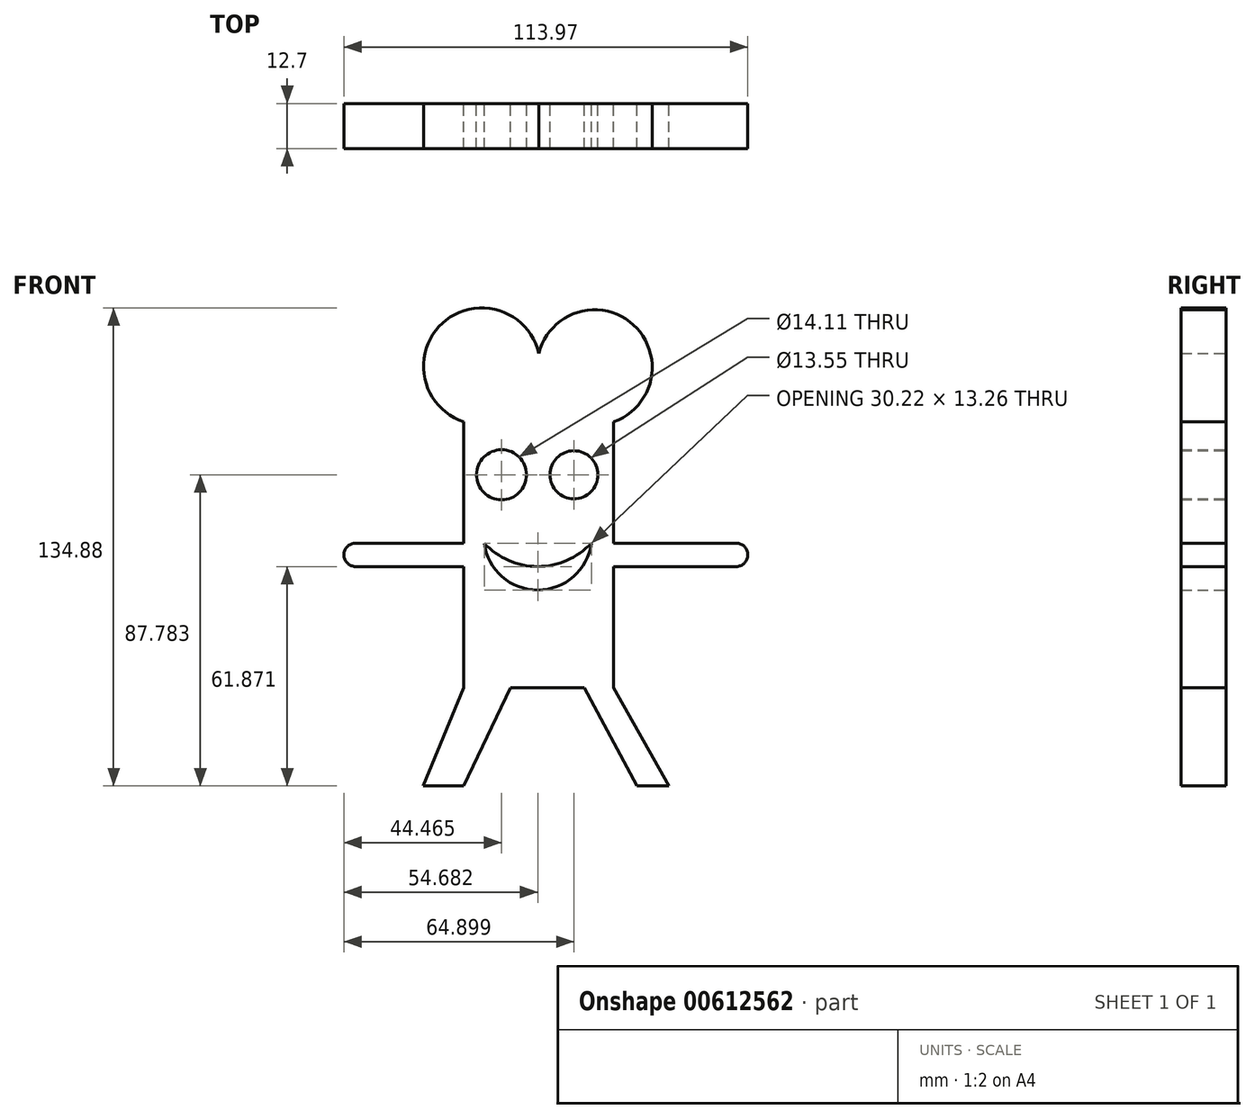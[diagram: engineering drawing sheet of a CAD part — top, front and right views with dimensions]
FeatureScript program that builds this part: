
annotation { "Feature Type Name" : "Feature", "Feature Type Description" : "" }
export const myFeature = defineFeature(function(context is Context, id is Id, definition is map)
    precondition{}
    {
        {
            var Q0;
            Q0=qCreatedBy(makeId("Front.planeOp"),FACE);
            var sketch = newSketch(context, id + "F0", { "sketchPlane" : qUnion([Q0])});
            skLineSegment(sketch, "E0.bottom", {"start": v(21.15, 37.56) * mm, "end": v(-21.15, 37.56) * mm});
            skLineSegment(sketch, "E0.top", {"start": v(21.15, -37.56) * mm, "end": v(-21.15, -37.56) * mm});
            skLineSegment(sketch, "E0.left", {"start": v(21.15, 37.56) * mm, "end": v(21.15, -37.56) * mm});
            skLineSegment(sketch, "E0.right", {"start": v(-21.15, 37.56) * mm, "end": v(-21.15, -37.56) * mm});
            skPoint(sketch, "E0.middle", {"position": v(0, 0) * mm});
            skArc(sketch, "E1", {"start": v(21.15, 37.56) * mm, "mid": v(26.71, 64.9) * mm, "end": v(0, 56.84) * mm});
            skPoint(sketch, "E1.endSnap0", {"position": v(0, 37.56) * mm});
            skArc(sketch, "E2", {"start": v(0, 56.84) * mm, "mid": v(-27.16, 65.4) * mm, "end": v(-21.15, 37.56) * mm});
            skCircle(sketch, "E3", {"center": v(-10.5, 22.6) * mm, "radius": 7.06 * mm});
            skCircle(sketch, "E4", {"center": v(9.93, 22.6) * mm, "radius": 6.77 * mm});
            skLineSegment(sketch, "E5.bottom", {"start": v(-21.15, 3.3) * mm, "end": v(-51.66, 3.3) * mm});
            skLineSegment(sketch, "E5.top", {"start": v(-21.15, -3.3) * mm, "end": v(-51.66, -3.3) * mm});
            skLineSegment(sketch, "E5.left", {"start": v(-21.15, 3.3) * mm, "end": v(-21.15, -3.3) * mm});
            skLineSegment(sketch, "E5.right", {"start": v(-51.66, 3.3) * mm, "end": v(-51.66, -3.3) * mm});
            skPoint(sketch, "E5.middle", {"position": v(-36.4, 0) * mm});
            skLineSegment(sketch, "E6.bottom", {"start": v(21.15, 3.3) * mm, "end": v(55.7, 3.3) * mm});
            skLineSegment(sketch, "E6.top", {"start": v(21.15, -3.3) * mm, "end": v(55.7, -3.3) * mm});
            skLineSegment(sketch, "E6.left", {"start": v(21.15, 3.3) * mm, "end": v(21.15, -3.3) * mm});
            skLineSegment(sketch, "E6.right", {"start": v(55.7, 3.3) * mm, "end": v(55.7, -3.3) * mm});
            skPoint(sketch, "E6.middle", {"position": v(38.42, 0) * mm});
            skArc(sketch, "E7", {"start": v(-51.66, 3.3) * mm, "mid": v(-54.97, 0) * mm, "end": v(-51.66, -3.3) * mm});
            skArc(sketch, "E8", {"start": v(55.7, -3.3) * mm, "mid": v(59, 0) * mm, "end": v(55.7, 3.3) * mm});
            skLineSegment(sketch, "E9", {"start": v(-21.15, -37.56) * mm, "end": v(-32.67, -65.19) * mm});
            skLineSegment(sketch, "E10", {"start": v(-32.67, -65.19) * mm, "end": v(-21.15, -65.19) * mm});
            skLineSegment(sketch, "E11", {"start": v(-21.15, -65.19) * mm, "end": v(-7.91, -37.56) * mm});
            skLineSegment(sketch, "E12", {"start": v(21.15, -37.56) * mm, "end": v(36.7, -65.19) * mm});
            skLineSegment(sketch, "E13", {"start": v(36.7, -65.19) * mm, "end": v(27.77, -65.19) * mm});
            skLineSegment(sketch, "E14", {"start": v(27.77, -65.19) * mm, "end": v(12.8, -37.56) * mm});
            skArc(sketch, "E15", {"start": v(-15.4, 3.3) * mm, "mid": v(-0.29, -9.95) * mm, "end": v(14.82, 3.3) * mm});
            skArc(sketch, "E16", {"start": v(-15.4, 3.3) * mm, "mid": v(-0.29, -3.29) * mm, "end": v(14.82, 3.3) * mm});
            skSolve(sketch);
        }
        {
            var Q0;
            Q0 = qSketchRegion(id + "F0", true);
            extrude(context, id + "F1", {"entities" : qUnion([Q0]), "depth" : 12.7 * mm, "offsetDistance" : 25.4 * mm});
        }
    });
